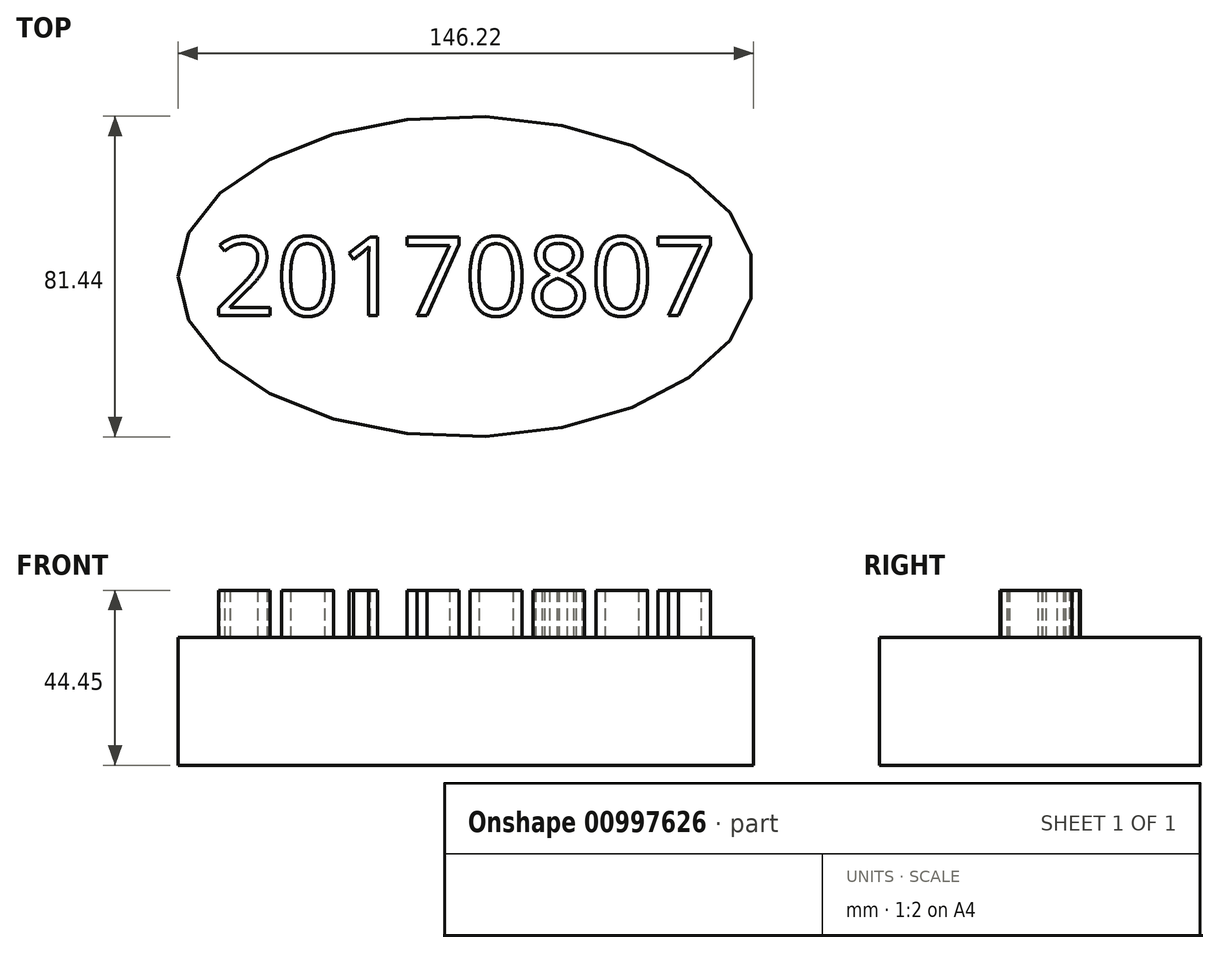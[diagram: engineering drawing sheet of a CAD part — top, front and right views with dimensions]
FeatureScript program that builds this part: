
annotation { "Feature Type Name" : "Feature", "Feature Type Description" : "" }
export const myFeature = defineFeature(function(context is Context, id is Id, definition is map)
    precondition{}
    {
        {
            var Q0;
            Q0=qCreatedBy(makeId("Top.planeOp"),FACE);
            var sketch = newSketch(context, id + "F0", { "sketchPlane" : qUnion([Q0])});
            skEllipse(sketch, "E0", {"center": v(0, 0) * mm, "majorRadius": 73.11 * mm, "minorRadius": 40.72 * mm, "majorAxis": v(-1, 0)});
            skSolve(sketch);
        }
        {
            var Q0;
            Q0=makeQuery(id+"F0.imprint","IMPRINT",FACE,{"disambiguationData":[TD([[makeQuery(id+"F0.imprint","IMPRINT",EDGE,{"derivedFrom":sQuery(id+"F0.wireOp",EDGE,"E0")}),1.0]])]});
            extrude(context, id + "F1", {"entities" : qUnion([Q0]), "depth" : 32.5 * mm, "offsetDistance" : 25.4 * mm});
        }
        {
            var Q0;
            Q0=makeQuery(id+"F1.opExtrude","CAP_FACE",FACE,{"disambiguationData":[OSD([sQuery(id+"F0.wireOp",EDGE,"E0")])],"isStart":false});
            var sketch = newSketch(context, id + "F2", { "sketchPlane" : qUnion([Q0])});
            skText(sketch, "E1", { "text": "20170807\n", "fontName": "OpenSans-Regular.ttf"});
            const initialGuessF2  = {"E1": [-0.06415, -0.00993, 1, 0, 0.0201]};
            skSetInitialGuess(sketch, initialGuessF2);
            skSolve(sketch);
        }
        {
            var Q0;
            Q0 = qSketchRegion(id + "F2", true);
            extrude(context, id + "F3", {"entities" : qUnion([Q0]), "operationType" : NewBodyOperationType.ADD, "depth" : 11.94 * mm, "offsetDistance" : 25.4 * mm});
        }
    });
